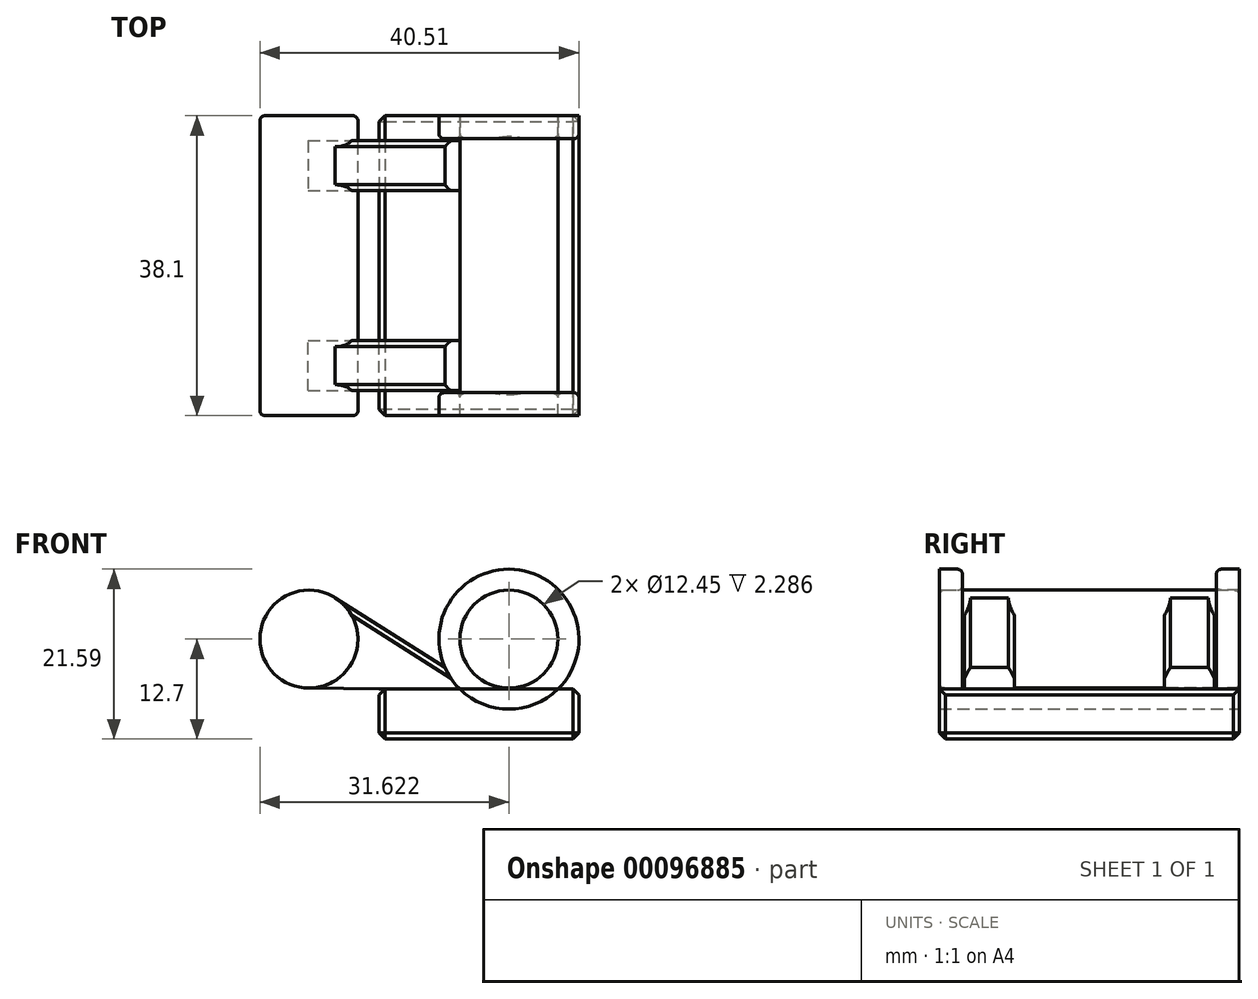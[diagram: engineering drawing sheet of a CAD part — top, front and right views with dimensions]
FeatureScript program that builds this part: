
annotation { "Feature Type Name" : "Feature", "Feature Type Description" : "" }
export const myFeature = defineFeature(function(context is Context, id is Id, definition is map)
    precondition{}
    {
        {
            var Q0;
            Q0=qCreatedBy(makeId("Front.planeOp"),FACE);
            var sketch = newSketch(context, id + "F0", { "sketchPlane" : qUnion([Q0])});
            skLineSegment(sketch, "E0.bottom", {"start": v(-20.32, -12.7) * mm, "end": v(-45.72, -12.7) * mm});
            skLineSegment(sketch, "E0.top", {"start": v(-20.32, -6.35) * mm, "end": v(-45.72, -6.35) * mm});
            skLineSegment(sketch, "E0.left", {"start": v(-20.32, -12.7) * mm, "end": v(-20.32, -6.35) * mm});
            skLineSegment(sketch, "E0.right", {"start": v(-45.72, -12.7) * mm, "end": v(-45.72, -6.35) * mm});
            skPoint(sketch, "E0.middle", {"position": v(-33.02, -9.53) * mm});
            skCircle(sketch, "E1", {"center": v(-54.6, 0) * mm, "radius": 6.22 * mm});
            skCircle(sketch, "E2", {"center": v(-29.2, 0) * mm, "radius": 6.22 * mm});
            skCircle(sketch, "E3", {"center": v(-29.2, 0) * mm, "radius": 8.9 * mm});
            skLineSegment(sketch, "E4", {"start": v(-54.7, -6.22) * mm, "end": v(-45.72, -6.35) * mm});
            skLineSegment(sketch, "E5", {"start": v(-51.27, 5.25) * mm, "end": v(-33.02, -6.35) * mm});
            skSolve(sketch);
        }
        {
            var Q0;
            {var subQ0=sQuery(id+"F0.wireOp",EDGE,"E3");var subQ1=sQuery(id+"F0.wireOp",EDGE,"E0.top");var subQ2=makeQuery(id+"F0.imprint","INTERSECT",VERTEX,{"disambiguationData":[OD(0.0)],"derivedFrom":[subQ1,subQ0]});Q0=makeQuery(id+"F0.imprint","IMPRINT",FACE,{"disambiguationData":[TD([[makeQuery(id+"F0.imprint","IMPRINT",EDGE,{"disambiguationData":[TD([[subQ2,-1.0]])],"derivedFrom":subQ1}),1.0]])]});}
            var Q1;
            Q1=makeQuery(id+"F0.imprint","IMPRINT",FACE,{"disambiguationData":[TD([[makeQuery(id+"F0.imprint","IMPRINT",EDGE,{"derivedFrom":sQuery(id+"F0.wireOp",EDGE,"E0.bottom")}),-1.0]])]});
            var Q2;
            {var subQ0=sQuery(id+"F0.wireOp",EDGE,"E1");var subQ1=makeQuery(id+"F0.imprint","INTERSECT",VERTEX,{"derivedFrom":[subQ0,sQuery(id+"F0.wireOp",EDGE,"E4")]});Q2=makeQuery(id+"F0.imprint","IMPRINT",FACE,{"disambiguationData":[TD([[makeQuery(id+"F0.imprint","IMPRINT",EDGE,{"disambiguationData":[TD([[subQ1,1.0]])],"derivedFrom":subQ0}),1.0]])]});}
            extrude(context, id + "F1", {"entities" : qUnion([Q0, Q1, Q2]), "endBound" : BoundingType.SYMMETRIC, "depth" : 38.1 * mm});
        }
        {
            var Q0;
            {var subQ0=sQuery(id+"F0.wireOp",EDGE,"E4");Q0=makeQuery(id+"F0.imprint","IMPRINT",FACE,{"disambiguationData":[TD([[makeQuery(id+"F0.imprint","IMPRINT",EDGE,{"derivedFrom":subQ0}),1.0]])]});}
            extrude(context, id + "F2", {"entities" : qUnion([Q0]), "endBound" : BoundingType.SYMMETRIC, "depth" : 19.05 * mm});
        }
        {
            var Q0;
            Q0=makeQuery(id+"F0.imprint","IMPRINT",FACE,{"disambiguationData":[TD([[makeQuery(id+"F0.imprint","IMPRINT",EDGE,{"derivedFrom":sQuery(id+"F0.wireOp",EDGE,"E2")}),-1.0]])]});
            var Q1;
            {var subQ0=sQuery(id+"F0.wireOp",EDGE,"E5");var subQ1=sQuery(id+"F0.wireOp",EDGE,"E0.top");var subQ2=makeQuery(id+"F0.imprint","INTERSECT",VERTEX,{"derivedFrom":[subQ1,subQ0]});Q1=makeQuery(id+"F0.imprint","IMPRINT",FACE,{"disambiguationData":[TD([[makeQuery(id+"F0.imprint","IMPRINT",EDGE,{"disambiguationData":[TD([[subQ2,-1.0]])],"derivedFrom":subQ1}),-1.0]])]});}
            extrude(context, id + "F3", {"entities" : qUnion([Q0, Q1]), "endBound" : BoundingType.SYMMETRIC, "depth" : 32.26 * mm});
        }
        {
            var Q0;
            Q0=makeQuery(id+"F3.opExtrude","CAP_FACE",FACE,{"disambiguationData":[OSD([sQuery(id+"F0.wireOp",EDGE,"E0.top"),sQuery(id+"F0.wireOp",EDGE,"E2"),sQuery(id+"F0.wireOp",EDGE,"E3")])],"isStart":false});
            var Q1;
            Q1=makeQuery(id+"F1.opExtrude","CAP_FACE",FACE,{"disambiguationData":[OSD([sQuery(id+"F0.wireOp",EDGE,"E0.bottom"),sQuery(id+"F0.wireOp",EDGE,"E0.top"),sQuery(id+"F0.wireOp",EDGE,"E0.left"),sQuery(id+"F0.wireOp",EDGE,"E0.right")])],"isStart":false});
            var Q2;
            Q2=makeQuery(id+"F1.opExtrude","SWEPT_BODY",BODY,{"disambiguationData":[OSD([sQuery(id+"F0.wireOp",EDGE,"E0.bottom"),sQuery(id+"F0.wireOp",EDGE,"E0.top"),sQuery(id+"F0.wireOp",EDGE,"E0.left"),sQuery(id+"F0.wireOp",EDGE,"E0.right")])]});
            extrude(context, id + "F4", {"entities" : qUnion([Q0]), "endBound" : BoundingType.UP_TO_SURFACE, "endBoundEntityFace" : qUnion([Q1]), "endBoundEntityBody" : qUnion([Q2]), "depth" : 2.95 * mm});
        }
        {
            var Q0;
            Q0=makeQuery(id+"F3.opExtrude","CAP_FACE",FACE,{"disambiguationData":[OSD([sQuery(id+"F0.wireOp",EDGE,"E0.top"),sQuery(id+"F0.wireOp",EDGE,"E2"),sQuery(id+"F0.wireOp",EDGE,"E3")])],"isStart":true});
            var Q1;
            Q1=makeQuery(id+"F1.opExtrude","CAP_FACE",FACE,{"disambiguationData":[OSD([sQuery(id+"F0.wireOp",EDGE,"E0.bottom"),sQuery(id+"F0.wireOp",EDGE,"E0.top"),sQuery(id+"F0.wireOp",EDGE,"E0.left"),sQuery(id+"F0.wireOp",EDGE,"E0.right")])],"isStart":true});
            extrude(context, id + "F5", {"entities" : qUnion([Q0]), "endBound" : BoundingType.UP_TO_SURFACE, "endBoundEntityFace" : qUnion([Q1]), "depth" : 25.4 * mm});
        }
        {
            var Q0;
            Q0=makeQuery(id+"F3.opExtrude","SWEPT_BODY",BODY,{"disambiguationData":[OSD([sQuery(id+"F0.wireOp",EDGE,"E0.top"),sQuery(id+"F0.wireOp",EDGE,"E2"),sQuery(id+"F0.wireOp",EDGE,"E3")])]});
            deleteBodies(context, id + "F6", {"entities" : qUnion([Q0])});
        }
        {
            var Q0;
            Q0=makeQuery(id+"F2.opExtrude","CAP_FACE",FACE,{"disambiguationData":[OSD([sQuery(id+"F0.wireOp",EDGE,"E0.top"),sQuery(id+"F0.wireOp",EDGE,"E1"),sQuery(id+"F0.wireOp",EDGE,"E3"),sQuery(id+"F0.wireOp",EDGE,"E4"),sQuery(id+"F0.wireOp",EDGE,"E5")])],"isStart":false});
            extrude(context, id + "F7", {"entities" : qUnion([Q0]), "depth" : 6.35 * mm});
        }
        {
            var Q0;
            Q0=makeQuery(id+"F2.opExtrude","CAP_FACE",FACE,{"disambiguationData":[OSD([sQuery(id+"F0.wireOp",EDGE,"E0.top"),sQuery(id+"F0.wireOp",EDGE,"E1"),sQuery(id+"F0.wireOp",EDGE,"E3"),sQuery(id+"F0.wireOp",EDGE,"E4"),sQuery(id+"F0.wireOp",EDGE,"E5")])],"isStart":true});
            extrude(context, id + "F8", {"entities" : qUnion([Q0]), "depth" : 6.35 * mm});
        }
        {
            var Q0;
            Q0=makeQuery(id+"F2.opExtrude","SWEPT_BODY",BODY,{"disambiguationData":[OSD([sQuery(id+"F0.wireOp",EDGE,"E0.top"),sQuery(id+"F0.wireOp",EDGE,"E1"),sQuery(id+"F0.wireOp",EDGE,"E3"),sQuery(id+"F0.wireOp",EDGE,"E4"),sQuery(id+"F0.wireOp",EDGE,"E5")])]});
            deleteBodies(context, id + "F9", {"entities" : qUnion([Q0])});
        }
        {
            var Q0;
            Q0=makeQuery(id+"F1.opExtrude","CAP_EDGE",EDGE,{"disambiguationData":[OSD([sQuery(id+"F0.wireOp",EDGE,"E1")])],"isStart":false});
            var Q1;
            Q1=makeQuery(id+"F1.opExtrude","CAP_EDGE",EDGE,{"disambiguationData":[OSD([sQuery(id+"F0.wireOp",EDGE,"E1")])],"isStart":true});
            var Q2;
            Q2=makeQuery(id+"F5.opExtrude","TWEAK_EDGE",EDGE,{"derivedFrom":[makeQuery(id+"F1.opExtrude","CAP_FACE",FACE,{"disambiguationData":[OSD([sQuery(id+"F0.wireOp",EDGE,"E0.bottom"),sQuery(id+"F0.wireOp",EDGE,"E0.top"),sQuery(id+"F0.wireOp",EDGE,"E0.left"),sQuery(id+"F0.wireOp",EDGE,"E0.right")])],"isStart":true}),makeQuery(id+"F3.opExtrude","CAP_EDGE",EDGE,{"disambiguationData":[OSD([sQuery(id+"F0.wireOp",EDGE,"E3")])],"isStart":true})]});
            var Q3;
            Q3=makeQuery(id+"F4.opExtrude","TWEAK_EDGE",EDGE,{"derivedFrom":[makeQuery(id+"F1.opExtrude","CAP_FACE",FACE,{"disambiguationData":[OSD([sQuery(id+"F0.wireOp",EDGE,"E0.bottom"),sQuery(id+"F0.wireOp",EDGE,"E0.top"),sQuery(id+"F0.wireOp",EDGE,"E0.left"),sQuery(id+"F0.wireOp",EDGE,"E0.right")])],"isStart":false}),makeQuery(id+"F3.opExtrude","CAP_EDGE",EDGE,{"disambiguationData":[OSD([sQuery(id+"F0.wireOp",EDGE,"E3")])],"isStart":false})]});
            var Q4;
            Q4=makeQuery(id+"F4.opExtrude","TWEAK_EDGE",EDGE,{"derivedFrom":[makeQuery(id+"F1.opExtrude","CAP_FACE",FACE,{"disambiguationData":[OSD([sQuery(id+"F0.wireOp",EDGE,"E0.bottom"),sQuery(id+"F0.wireOp",EDGE,"E0.top"),sQuery(id+"F0.wireOp",EDGE,"E0.left"),sQuery(id+"F0.wireOp",EDGE,"E0.right")])],"isStart":false}),makeQuery(id+"F3.opExtrude","CAP_EDGE",EDGE,{"disambiguationData":[OSD([sQuery(id+"F0.wireOp",EDGE,"E2")])],"isStart":false})]});
            var Q5;
            Q5=makeQuery(id+"F4.opExtrude","CAP_EDGE",EDGE,{"disambiguationData":[OSD([sQuery(id+"F0.wireOp",EDGE,"E2")])],"isStart":true});
            var Q6;
            Q6=makeQuery(id+"F4.opExtrude","CAP_EDGE",EDGE,{"disambiguationData":[OSD([sQuery(id+"F0.wireOp",EDGE,"E3")])],"isStart":true});
            var Q7;
            Q7=makeQuery(id+"F5.opExtrude","CAP_EDGE",EDGE,{"disambiguationData":[OSD([sQuery(id+"F0.wireOp",EDGE,"E2")])],"isStart":true});
            var Q8;
            Q8=makeQuery(id+"F5.opExtrude","CAP_EDGE",EDGE,{"disambiguationData":[OSD([sQuery(id+"F0.wireOp",EDGE,"E3")])],"isStart":true});
            var Q9;
            Q9=makeQuery(id+"F5.opExtrude","TWEAK_EDGE",EDGE,{"derivedFrom":[makeQuery(id+"F1.opExtrude","CAP_FACE",FACE,{"disambiguationData":[OSD([sQuery(id+"F0.wireOp",EDGE,"E0.bottom"),sQuery(id+"F0.wireOp",EDGE,"E0.top"),sQuery(id+"F0.wireOp",EDGE,"E0.left"),sQuery(id+"F0.wireOp",EDGE,"E0.right")])],"isStart":true}),makeQuery(id+"F3.opExtrude","CAP_EDGE",EDGE,{"disambiguationData":[OSD([sQuery(id+"F0.wireOp",EDGE,"E2")])],"isStart":true})]});
            fillet(context, id + "F10", {"entities" : qUnion([Q0, Q1, Q2, Q3, Q4, Q5, Q6, Q7, Q8, Q9]), "radius" : 0.64 * mm, "tangentPropagation" : true, "allowEdgeOverflow" : false});
        }
        {
            var Q0;
            Q0=makeQuery(id+"F7.opExtrude","CAP_EDGE",EDGE,{"disambiguationData":[OSD([sQuery(id+"F0.wireOp",EDGE,"E5")])],"isStart":false});
            var Q1;
            Q1=makeQuery(id+"F7.opExtrude","CAP_EDGE",EDGE,{"disambiguationData":[OSD([sQuery(id+"F0.wireOp",EDGE,"E5")])],"isStart":true});
            var Q2;
            Q2=makeQuery(id+"F8.opExtrude","CAP_EDGE",EDGE,{"disambiguationData":[OSD([sQuery(id+"F0.wireOp",EDGE,"E5")])],"isStart":true});
            var Q3;
            Q3=makeQuery(id+"F8.opExtrude","CAP_EDGE",EDGE,{"disambiguationData":[OSD([sQuery(id+"F0.wireOp",EDGE,"E5")])],"isStart":false});
            var Q4;
            Q4=makeQuery(id+"F1.opExtrude","SWEPT_FACE",FACE,{"disambiguationData":[OSD([sQuery(id+"F0.wireOp",EDGE,"E0.bottom")])]});
            var Q5;
            Q5=makeQuery(id+"F1.opExtrude","SWEPT_FACE",FACE,{"disambiguationData":[OSD([sQuery(id+"F0.wireOp",EDGE,"E0.left")])]});
            var Q6;
            Q6=makeQuery(id+"F1.opExtrude","SWEPT_FACE",FACE,{"disambiguationData":[OSD([sQuery(id+"F0.wireOp",EDGE,"E0.right")])]});
            chamfer(context, id + "F11", {"entities" : qUnion([Q0, Q1, Q2, Q3, Q4, Q5, Q6]), "width" : 0.76 * mm, "tangentPropagation" : true});
        }
    });
